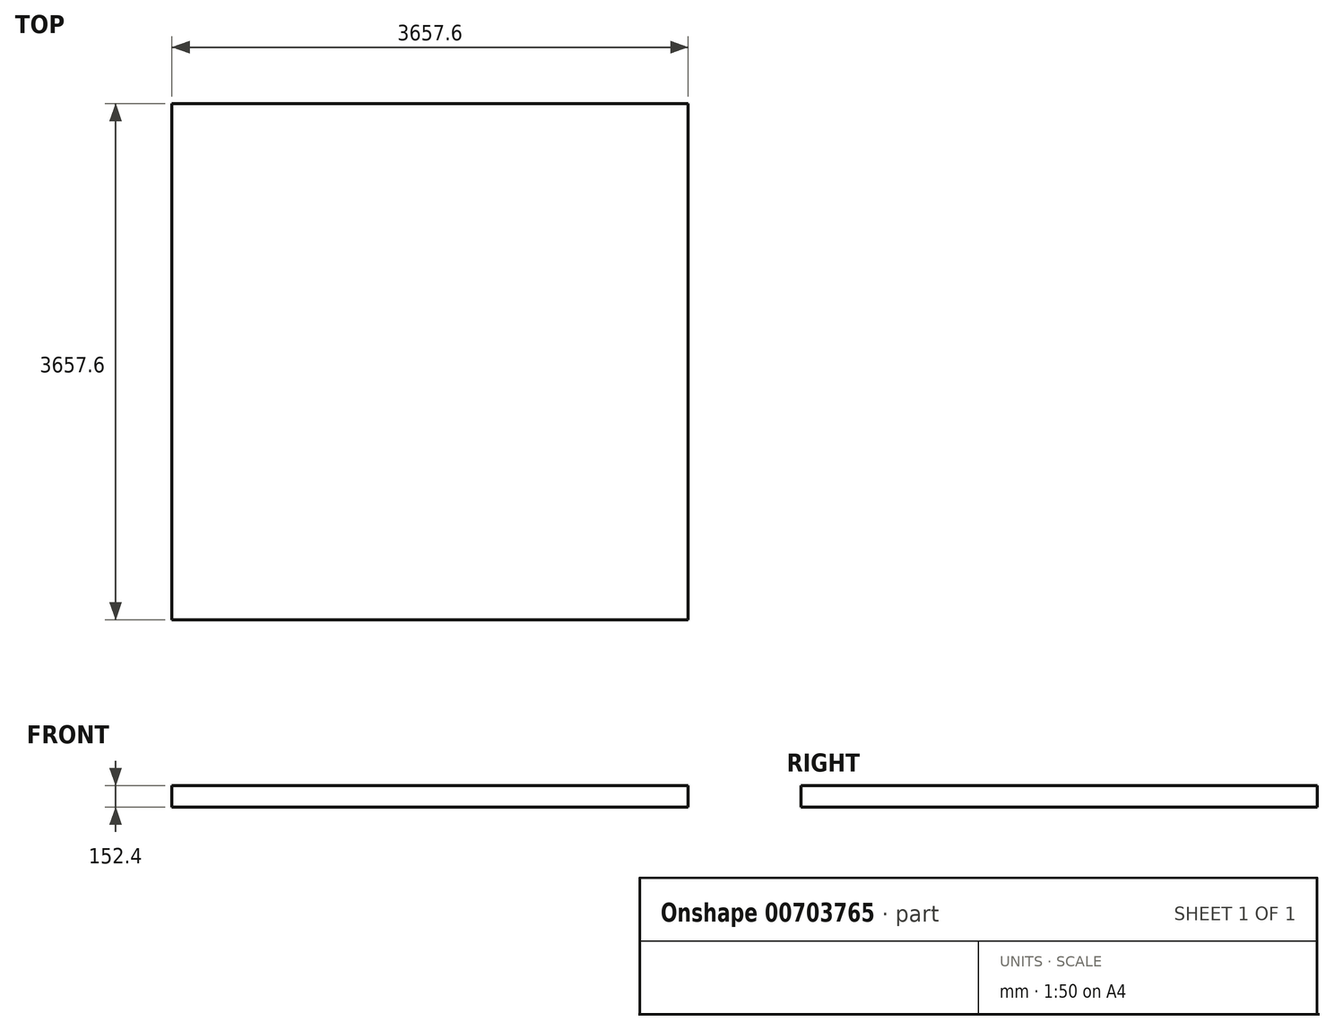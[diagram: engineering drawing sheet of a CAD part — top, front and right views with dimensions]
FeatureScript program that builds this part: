
annotation { "Feature Type Name" : "Feature", "Feature Type Description" : "" }
export const myFeature = defineFeature(function(context is Context, id is Id, definition is map)
    precondition{}
    {
        {
            var Q0;
            Q0=qCreatedBy(makeId("Top.planeOp"),FACE);
            var sketch = newSketch(context, id + "F0", { "sketchPlane" : qUnion([Q0])});
            skLineSegment(sketch, "E0.bottom", {"start": v(0, 3657.6) * mm, "end": v(3657.6, 3657.6) * mm});
            skLineSegment(sketch, "E0.top", {"start": v(0, 0) * mm, "end": v(3657.6, 0) * mm});
            skLineSegment(sketch, "E0.left", {"start": v(0, 3657.6) * mm, "end": v(0, 0) * mm});
            skLineSegment(sketch, "E0.right", {"start": v(3657.6, 3657.6) * mm, "end": v(3657.6, 0) * mm});
            skSolve(sketch);
        }
        {
            var Q0;
            Q0=makeQuery(id+"F0.imprint","IMPRINT",FACE,{"disambiguationData":[TD([[makeQuery(id+"F0.imprint","IMPRINT",EDGE,{"derivedFrom":sQuery(id+"F0.wireOp",EDGE,"E0.bottom")}),-1.0]])]});
            extrude(context, id + "F1", {"entities" : qUnion([Q0]), "depth" : 152.4 * mm, "offsetDistance" : 25.4 * mm});
        }
    });
